# Revit family: apollon_r__21_linear_51mq18w72414_9133
name_source: partatom
category: Lighting Fixtures
units: mm (PartAtom-declared; Revit-internal decimal feet)

## family parameters
Cut with Voids When Loaded = No
Host = Face
Light Source = No
Part Type = Normal
Room Calculation Point = No
Round Connector Dimension = Use Diameter
Shared = No

## types (1)
- Apollon® 21 linear (1 x LED, 3820 lm, 21.9 W, 4000K)
    Apparent Load = 22 VA
    CIE Flux Codes = 60 87 97 100 100
    Color Rendering = 80
    Color Temperature = 4000K
    Default Elevation = 1800 mm
    Description = Apollon® 21 linear, office luminaire, primary optical cover: micro prismatic cover, of PMMA, CAT 2 (L<= 3000cd/m²), light emission: direct distribution, primary light characteristic: symmetric, installation type: lay-in mounting, LED, rated luminous flux: 3.820lm, luminous efficacy: 175lm/W, light colour: 840, colour temperature: 4000K, with terminal, 3-pole, mains connection: 220..240V, AC/DC, 0/50..60Hz, rated input power: 21.9W, housing, of aluminium, coated, traffic white (RAL 9016), length: 1.195mm, width: 295mm, height: 30mm, housing upper side, of sheet steel, galvanised, protection rating (complete): IP20, protection rating (lamp compartment, on room side): IP50, insulation class (complete): insulation class II (safety insulation), certification: CE, ENEC, impact resistance: IK03, permissible operating ambient temperature: -20..+45°C, permissible storage temperature: -40..+80°C, packaging unit: 1 piece
    Height = 0 mm  [stored 0 ft]
    Lamp = 1 x LED
    Lamp Light Flux = 3820 lm
    Lamp Power = 21.9 W
    Lamp count = 1
    Length = 1195 mm
    Luminous efficacy = 174 lm/W
    Manufacturer = Siteco
    ModVariant = No
    Model = 51MQ18W72414
    Mounting Place = Ceiling
    Mounting Type = Recessed
    Number of Poles = 1
    OnlyDefault = Yes
    Power Factor = 1
    Product Name = Apollon® 21 linear
    Product group = office luminaire | ceiling recessed
    ProductGroupID = 401
    Protection Class = Protection class II
    Protection Degree = IP 20
    RLX_Detail_Level = 1
    RLX_Emergency_Light_Flux = 0 lm
    RLX_Emergency_Type = 0
    RLX_Emergency_Type_DB = No
    RlxData = <blob elided: 15233 chars, md5=8dd8ee23>
    Socket = socket
    Standby Power = 0 W
    System Light Flux = 3820 lm
    System Power = 22 W
    Type Comments = Product without accessories
    Type Image = l_1291045.jpg
    URL = http://relux.com
    VarID = ---
    Voltage = 0 V
    Weight = 0.00 kg
    Width = 295 mm

note: [stored X ft] marks values corroborated as IEEE doubles in the binary element streams (Revit-internal decimal feet)

## geometry (parser evidence)
native form markers: Blend x4, Sweep x12
no freeform markers — native parametric forms only
